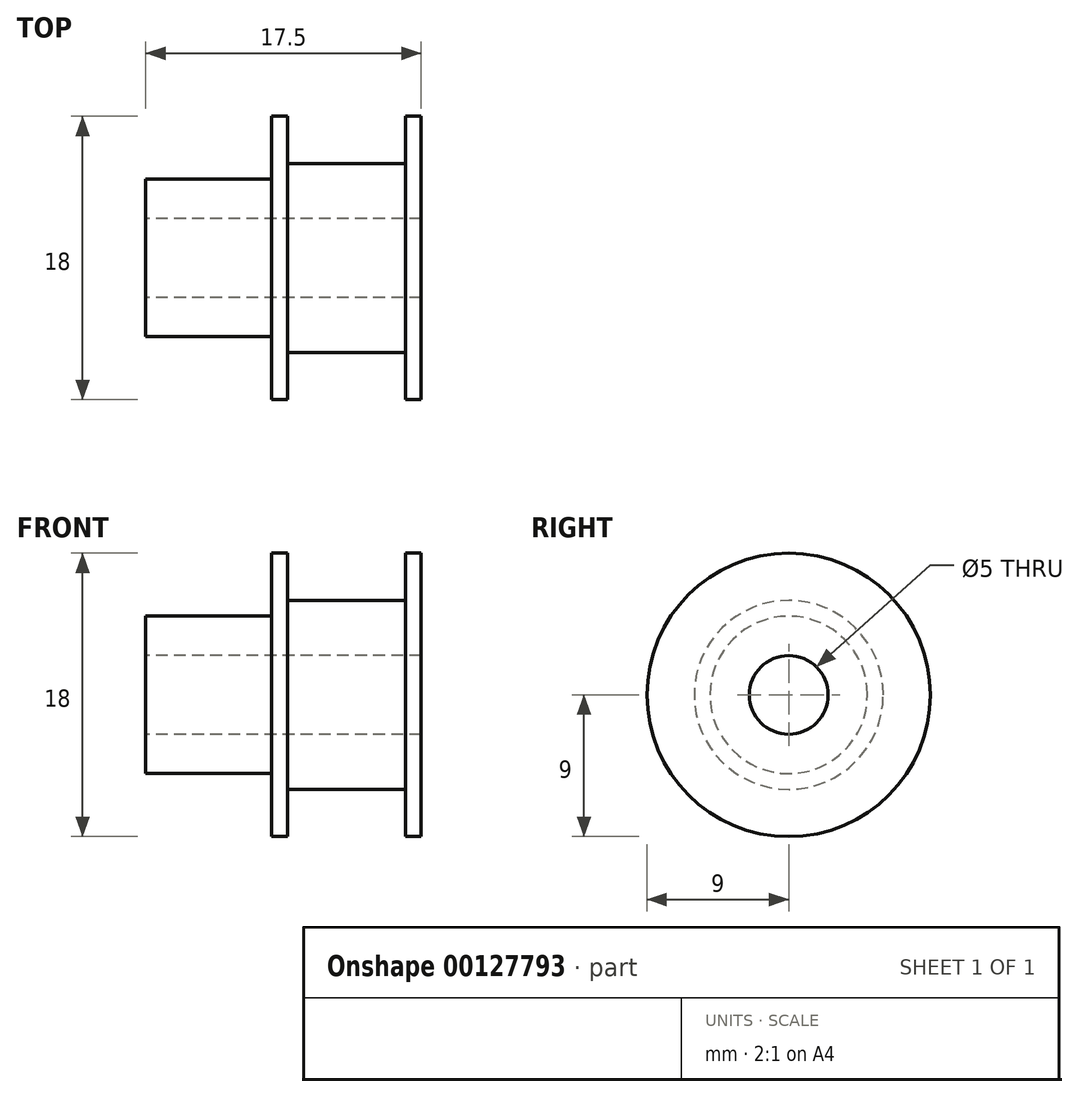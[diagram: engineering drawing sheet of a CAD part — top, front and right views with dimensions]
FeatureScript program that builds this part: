
annotation { "Feature Type Name" : "Feature", "Feature Type Description" : "" }
export const myFeature = defineFeature(function(context is Context, id is Id, definition is map)
    precondition{}
    {
        {
            var Q0;
            Q0=qCreatedBy(makeId("Front.planeOp"),FACE);
            var sketch = newSketch(context, id + "F0", { "sketchPlane" : qUnion([Q0])});
            skLineSegment(sketch, "E0", {"start": v(0, 0) * mm, "end": v(0, 5) * mm});
            skLineSegment(sketch, "E1", {"start": v(0, 5) * mm, "end": v(8, 5) * mm});
            skLineSegment(sketch, "E2", {"start": v(8, 5) * mm, "end": v(8, 9) * mm});
            skLineSegment(sketch, "E3", {"start": v(8, 9) * mm, "end": v(9, 9) * mm});
            skLineSegment(sketch, "E4", {"start": v(9, 9) * mm, "end": v(9, 6) * mm});
            skLineSegment(sketch, "E5", {"start": v(9, 6) * mm, "end": v(16.5, 6) * mm});
            skLineSegment(sketch, "E6", {"start": v(16.5, 6) * mm, "end": v(16.5, 9) * mm});
            skLineSegment(sketch, "E7", {"start": v(16.5, 9) * mm, "end": v(17.5, 9) * mm});
            skLineSegment(sketch, "E8", {"start": v(17.5, 9) * mm, "end": v(17.5, 0) * mm});
            skLineSegment(sketch, "E9", {"start": v(17.5, 0) * mm, "end": v(0, 0) * mm});
            skLineSegment(sketch, "E10", {"start": v(0, 0) * mm, "end": v(-15.59, 0) * mm, "construction": true});
            skSolve(sketch);
        }
        {
            var Q0;
            Q0 = qSketchRegion(id + "F0", true);
            var Q1;
            Q1=sQuery(id+"F0.wireOp",EDGE,"E10");
            revolve(context, id + "F1", {"entities" : qUnion([Q0]), "axis" : qUnion([Q1]), "revolveType" : RevolveType.FULL});
        }
        {
            var Q0;
            Q0=makeQuery(id+"F1.opRevolve","SWEPT_FACE",FACE,{"disambiguationData":[OSD([sQuery(id+"F0.wireOp",EDGE,"E0")])]});
            var sketch = newSketch(context, id + "F2", { "sketchPlane" : qUnion([Q0])});
            skCircle(sketch, "E11", {"center": v(0, 0) * mm, "radius": 2.5 * mm});
            skSolve(sketch);
        }
        {
            var Q0;
            Q0 = qSketchRegion(id + "F2", true);
            extrude(context, id + "F3", {"entities" : qUnion([Q0]), "operationType" : NewBodyOperationType.REMOVE, "endBound" : BoundingType.THROUGH_ALL, "oppositeDirection" : true, "depth" : 25 * mm});
        }
    });
